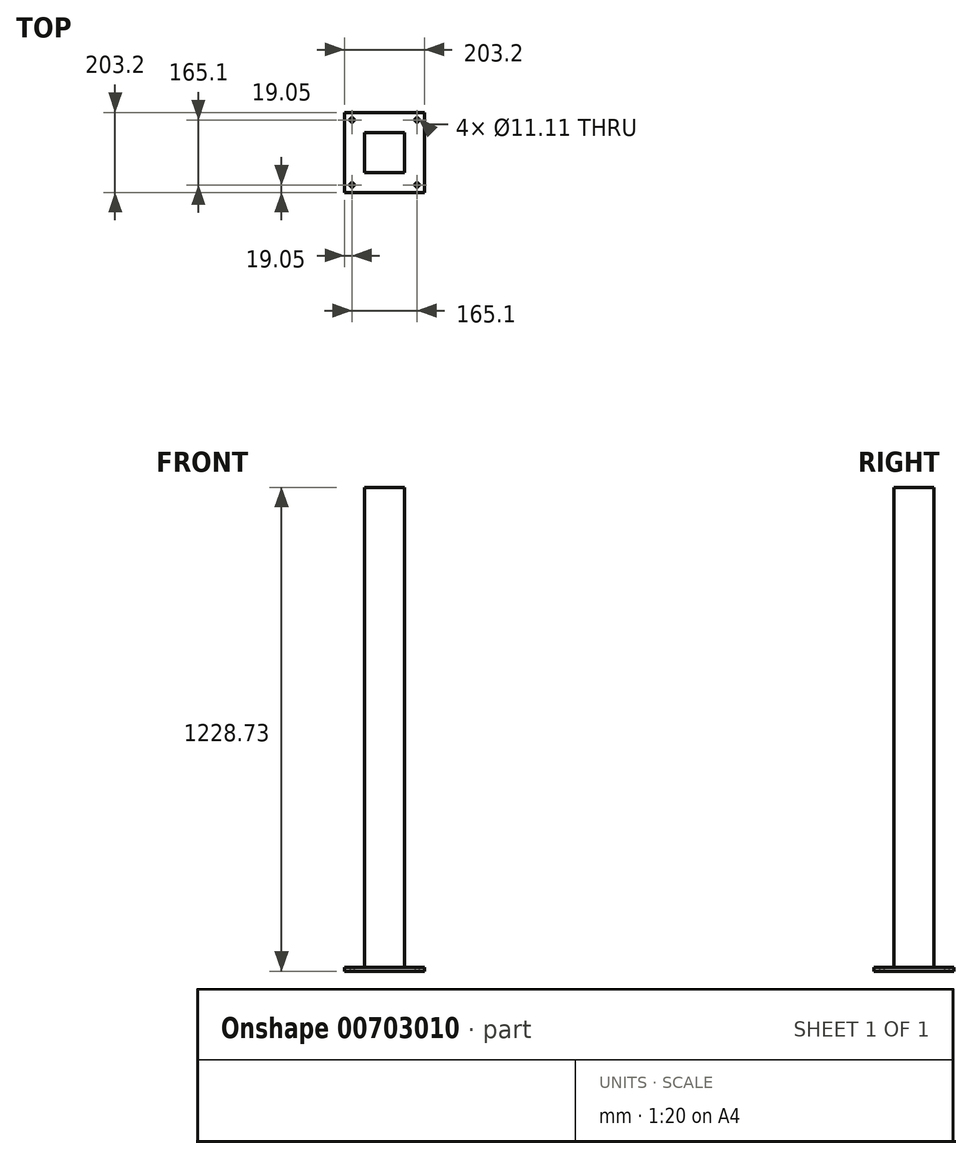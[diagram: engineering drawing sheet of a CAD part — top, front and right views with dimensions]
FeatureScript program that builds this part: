
annotation { "Feature Type Name" : "Feature", "Feature Type Description" : "" }
export const myFeature = defineFeature(function(context is Context, id is Id, definition is map)
    precondition{}
    {
        {
            var Q0;
            Q0=qCreatedBy(makeId("Top.planeOp"),FACE);
            var sketch = newSketch(context, id + "F0", { "sketchPlane" : qUnion([Q0])});
            skLineSegment(sketch, "E0.bottom", {"start": v(-101.6, -101.6) * mm, "end": v(101.6, -101.6) * mm});
            skLineSegment(sketch, "E0.top", {"start": v(-101.6, 101.6) * mm, "end": v(101.6, 101.6) * mm});
            skLineSegment(sketch, "E0.left", {"start": v(-101.6, -101.6) * mm, "end": v(-101.6, 101.6) * mm});
            skLineSegment(sketch, "E0.right", {"start": v(101.6, -101.6) * mm, "end": v(101.6, 101.6) * mm});
            skPoint(sketch, "E0.middle", {"position": v(0, 0) * mm});
            skPoint(sketch, "E1", {"position": v(-82.55, 82.55) * mm});
            skPoint(sketch, "E2", {"position": v(82.55, 82.55) * mm});
            skPoint(sketch, "E3", {"position": v(82.55, -82.55) * mm});
            skPoint(sketch, "E4", {"position": v(-82.55, -82.55) * mm});
            skSolve(sketch);
        }
        {
            var Q0;
            Q0=makeQuery(id+"F0.imprint","IMPRINT",FACE,{"disambiguationData":[TD([[makeQuery(id+"F0.imprint","IMPRINT",EDGE,{"derivedFrom":sQuery(id+"F0.wireOp",EDGE,"E0.bottom")}),1.0]])]});
            extrude(context, id + "F1", {"entities" : qUnion([Q0]), "depth" : 9.52 * mm, "offsetDistance" : 25.4 * mm});
        }
        {
            var Q0;
            Q0=makeQuery(id+"F1.opExtrude","CAP_FACE",FACE,{"disambiguationData":[OSD([sQuery(id+"F0.wireOp",EDGE,"E0.bottom"),sQuery(id+"F0.wireOp",EDGE,"E0.top"),sQuery(id+"F0.wireOp",EDGE,"E0.left"),sQuery(id+"F0.wireOp",EDGE,"E0.right")])],"isStart":false});
            var sketch = newSketch(context, id + "F2", { "sketchPlane" : qUnion([Q0])});
            skLineSegment(sketch, "E5.bottom", {"start": v(50.8, 50.8) * mm, "end": v(-50.8, 50.8) * mm});
            skLineSegment(sketch, "E5.top", {"start": v(50.8, -50.8) * mm, "end": v(-50.8, -50.8) * mm});
            skLineSegment(sketch, "E5.left", {"start": v(50.8, 50.8) * mm, "end": v(50.8, -50.8) * mm});
            skLineSegment(sketch, "E5.right", {"start": v(-50.8, 50.8) * mm, "end": v(-50.8, -50.8) * mm});
            skPoint(sketch, "E5.middle", {"position": v(0, 0) * mm});
            skSolve(sketch);
        }
        {
            var Q0;
            Q0=sQuery(id+"F0.wireOp",VERTEX,"E1");
            var Q1;
            Q1=sQuery(id+"F0.wireOp",VERTEX,"E2");
            var Q2;
            Q2=sQuery(id+"F0.wireOp",VERTEX,"E3");
            var Q3;
            Q3=sQuery(id+"F0.wireOp",VERTEX,"E4");
            var Q4;
            Q4=makeQuery(id+"F1.opExtrude","SWEPT_BODY",BODY,{"disambiguationData":[OSD([sQuery(id+"F0.wireOp",EDGE,"E0.bottom"),sQuery(id+"F0.wireOp",EDGE,"E0.top"),sQuery(id+"F0.wireOp",EDGE,"E0.left"),sQuery(id+"F0.wireOp",EDGE,"E0.right")])]});
            hole(context, id + "F3", {"style" : HoleStyle.SIMPLE, "endStyle" : HoleEndStyle.THROUGH, "oppositeDirection" : true, "holeDiameter" : 11.1 * mm, "majorDiameter" : 6.35 * mm, "isTappedThrough" : true, "tappedDepth" : 12.7 * mm, "tapClearance" : 3, "locations" : qUnion([Q0, Q1, Q2, Q3]), "scope" : qUnion([Q4])});
        }
        {
            var Q0;
            Q0=makeQuery(id+"F2.imprint","IMPRINT",FACE,{"disambiguationData":[TD([[makeQuery(id+"F2.imprint","IMPRINT",EDGE,{"derivedFrom":sQuery(id+"F2.wireOp",EDGE,"E5.bottom")}),1.0]])]});
            extrude(context, id + "F4", {"entities" : qUnion([Q0]), "depth" : 1219.2 * mm, "offsetDistance" : 25.4 * mm});
        }
    });
